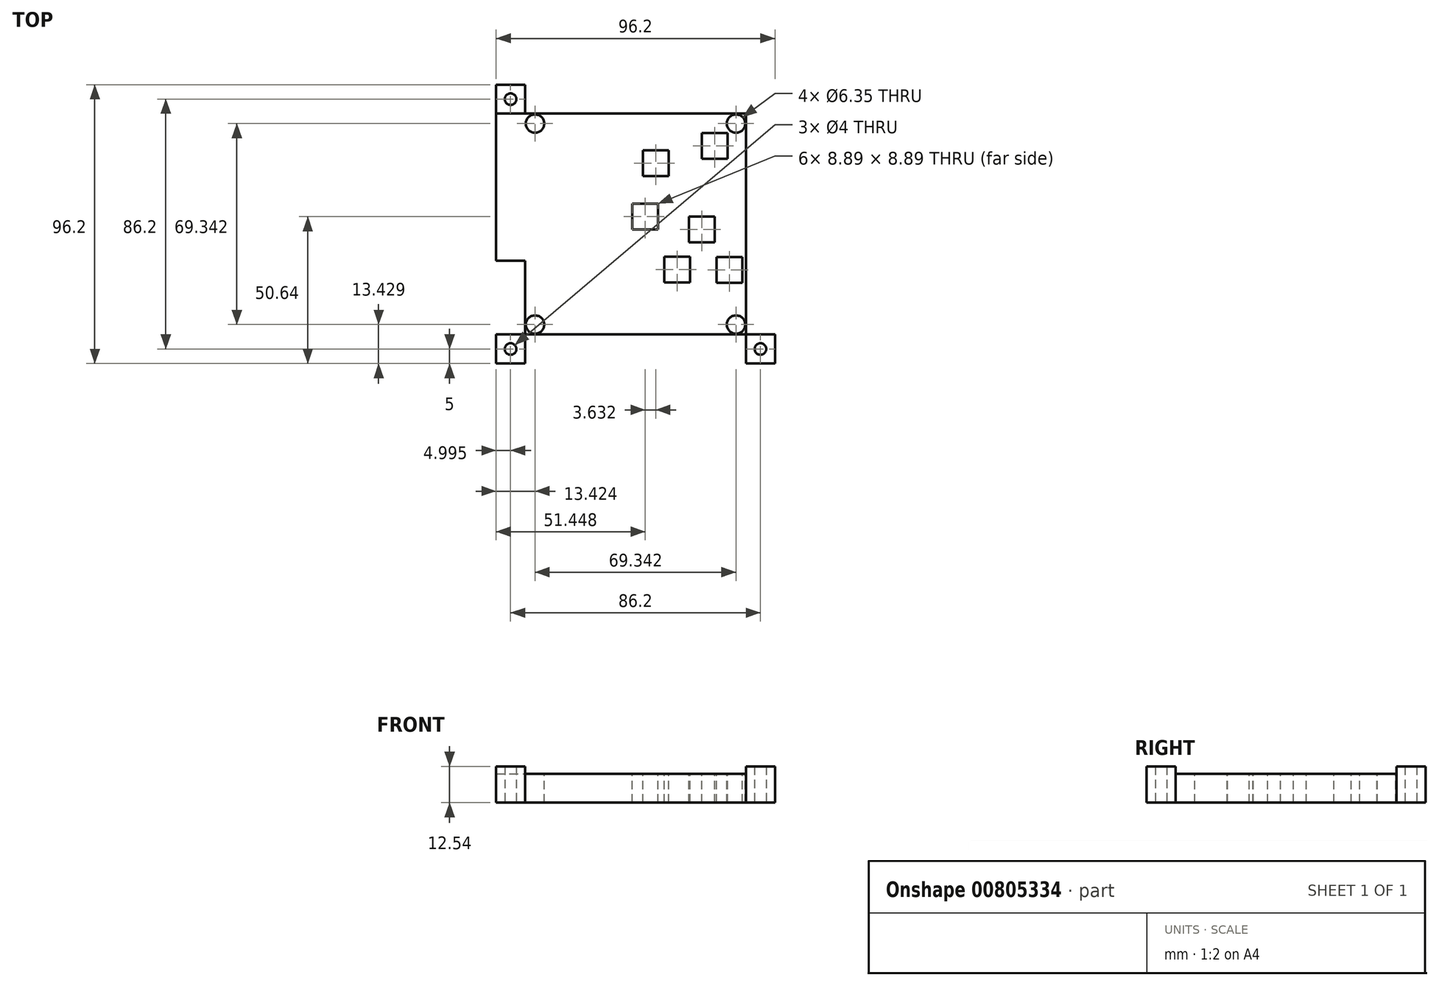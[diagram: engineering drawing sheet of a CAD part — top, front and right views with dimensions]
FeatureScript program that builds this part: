
annotation { "Feature Type Name" : "Feature", "Feature Type Description" : "" }
export const myFeature = defineFeature(function(context is Context, id is Id, definition is map)
    precondition{}
    {
        {
            var Q0;
            Q0=qCreatedBy(makeId("Top.planeOp"),FACE);
            var sketch = newSketch(context, id + "F0", { "sketchPlane" : qUnion([Q0])});
            skLineSegment(sketch, "E0.bottom", {"start": v(-59.12, -65.9) * mm, "end": v(37.08, -65.9) * mm});
            skLineSegment(sketch, "E0.top", {"start": v(-59.12, 30.3) * mm, "end": v(37.08, 30.3) * mm});
            skLineSegment(sketch, "E0.left", {"start": v(-59.12, -65.9) * mm, "end": v(-59.12, 30.3) * mm});
            skLineSegment(sketch, "E0.right", {"start": v(37.08, -65.9) * mm, "end": v(37.08, 30.3) * mm});
            skLineSegment(sketch, "E1.bottom", {"start": v(-59.12, -65.9) * mm, "end": v(-49.12, -65.9) * mm});
            skLineSegment(sketch, "E1.top", {"start": v(-59.12, -55.9) * mm, "end": v(-49.12, -55.9) * mm});
            skLineSegment(sketch, "E1.left", {"start": v(-59.12, -65.9) * mm, "end": v(-59.12, -55.9) * mm});
            skLineSegment(sketch, "E1.right", {"start": v(-49.12, -65.9) * mm, "end": v(-49.12, -55.9) * mm});
            skLineSegment(sketch, "E2.bottom", {"start": v(-49.12, -55.9) * mm, "end": v(27.08, -55.9) * mm});
            skLineSegment(sketch, "E2.top", {"start": v(-49.12, 20.3) * mm, "end": v(27.08, 20.3) * mm});
            skLineSegment(sketch, "E2.left", {"start": v(-49.12, -55.9) * mm, "end": v(-49.12, 20.3) * mm});
            skLineSegment(sketch, "E2.right", {"start": v(27.08, -55.9) * mm, "end": v(27.08, 20.3) * mm});
            skLineSegment(sketch, "E3.bottom", {"start": v(37.08, -65.9) * mm, "end": v(27.08, -65.9) * mm});
            skLineSegment(sketch, "E3.top", {"start": v(37.08, -55.9) * mm, "end": v(27.08, -55.9) * mm});
            skLineSegment(sketch, "E3.left", {"start": v(37.08, -65.9) * mm, "end": v(37.08, -55.9) * mm});
            skLineSegment(sketch, "E3.right", {"start": v(27.08, -65.9) * mm, "end": v(27.08, -55.9) * mm});
            skLineSegment(sketch, "E4.bottom", {"start": v(37.08, 30.3) * mm, "end": v(27.08, 30.3) * mm});
            skLineSegment(sketch, "E4.top", {"start": v(37.08, 20.3) * mm, "end": v(27.08, 20.3) * mm});
            skLineSegment(sketch, "E4.left", {"start": v(37.08, 30.3) * mm, "end": v(37.08, 20.3) * mm});
            skLineSegment(sketch, "E4.right", {"start": v(27.08, 30.3) * mm, "end": v(27.08, 20.3) * mm});
            skLineSegment(sketch, "E5.bottom", {"start": v(-59.12, 30.3) * mm, "end": v(-49.12, 30.3) * mm});
            skLineSegment(sketch, "E5.top", {"start": v(-59.12, 20.3) * mm, "end": v(-49.12, 20.3) * mm});
            skLineSegment(sketch, "E5.left", {"start": v(-59.12, 30.3) * mm, "end": v(-59.12, 20.3) * mm});
            skLineSegment(sketch, "E5.right", {"start": v(-49.12, 30.3) * mm, "end": v(-49.12, 20.3) * mm});
            skLineSegment(sketch, "E6.bottom", {"start": v(-59.12, 20.3) * mm, "end": v(-54.12, 20.3) * mm});
            skLineSegment(sketch, "E6.left", {"start": v(-59.12, 20.3) * mm, "end": v(-59.12, 25.3) * mm});
            skLineSegment(sketch, "E7.bottom", {"start": v(37.08, 20.3) * mm, "end": v(32.08, 20.3) * mm});
            skLineSegment(sketch, "E7.left", {"start": v(37.08, 20.3) * mm, "end": v(37.08, 25.3) * mm});
            skLineSegment(sketch, "E8.bottom", {"start": v(-59.12, -65.9) * mm, "end": v(-54.12, -65.9) * mm});
            skLineSegment(sketch, "E8.left", {"start": v(-59.12, -65.9) * mm, "end": v(-59.12, -60.9) * mm});
            skLineSegment(sketch, "E9.bottom", {"start": v(37.08, -65.9) * mm, "end": v(32.08, -65.9) * mm});
            skLineSegment(sketch, "E9.left", {"start": v(37.08, -65.9) * mm, "end": v(37.08, -60.9) * mm});
            skCircle(sketch, "E10", {"center": v(-54.12, 25.3) * mm, "radius": 2 * mm});
            skCircle(sketch, "E11", {"center": v(32.08, 25.3) * mm, "radius": 2 * mm});
            skCircle(sketch, "E12", {"center": v(-54.12, -60.9) * mm, "radius": 2 * mm});
            skCircle(sketch, "E13", {"center": v(32.08, -60.9) * mm, "radius": 2 * mm});
            skLineSegment(sketch, "E14.left", {"start": v(-49.12, -55.9) * mm, "end": v(-49.12, -55.65) * mm});
            skLineSegment(sketch, "E14.right", {"start": v(27.08, -55.9) * mm, "end": v(27.08, -55.65) * mm});
            skLineSegment(sketch, "E15.bottom", {"start": v(-49.12, 20.3) * mm, "end": v(-48.87, 20.3) * mm});
            skLineSegment(sketch, "E15.top", {"start": v(-49.12, -55.9) * mm, "end": v(-48.87, -55.9) * mm});
            skLineSegment(sketch, "E16.left", {"start": v(-49.12, 20.3) * mm, "end": v(-49.12, 20.05) * mm});
            skLineSegment(sketch, "E16.right", {"start": v(27.08, 20.3) * mm, "end": v(27.08, 20.05) * mm});
            skLineSegment(sketch, "E17.bottom", {"start": v(27.08, 20.3) * mm, "end": v(26.82, 20.3) * mm});
            skLineSegment(sketch, "E17.top", {"start": v(27.08, -55.9) * mm, "end": v(26.82, -55.9) * mm});
            skLineSegment(sketch, "E17.left", {"start": v(27.08, 20.3) * mm, "end": v(27.08, -55.9) * mm});
            skLineSegment(sketch, "E18.bottom", {"start": v(-49.12, -55.9) * mm, "end": v(-45.19, -55.9) * mm});
            skLineSegment(sketch, "E19.left", {"start": v(-49.12, -55.9) * mm, "end": v(-49.12, -54.15) * mm});
            skLineSegment(sketch, "E20.left", {"start": v(-49.12, -55.9) * mm, "end": v(-49.12, -51.96) * mm});
            skLineSegment(sketch, "E21.left", {"start": v(27.08, -55.9) * mm, "end": v(27.08, -51.96) * mm});
            skLineSegment(sketch, "E22.bottom", {"start": v(27.2, -55.9) * mm, "end": v(27.08, -55.9) * mm});
            skLineSegment(sketch, "E23.bottom", {"start": v(27.08, -55.9) * mm, "end": v(23.14, -55.9) * mm});
            skLineSegment(sketch, "E24.left", {"start": v(-49.12, 20.3) * mm, "end": v(-49.12, 16.36) * mm});
            skLineSegment(sketch, "E25.bottom", {"start": v(-49.12, 20.3) * mm, "end": v(-45.19, 20.3) * mm});
            skLineSegment(sketch, "E26.bottom", {"start": v(27.32, 20.3) * mm, "end": v(27.08, 20.3) * mm});
            skLineSegment(sketch, "E26.left", {"start": v(27.08, 20.43) * mm, "end": v(27.08, 20.3) * mm});
            skLineSegment(sketch, "E26.right", {"start": v(27.32, 20.43) * mm, "end": v(27.32, 20.3) * mm});
            skLineSegment(sketch, "E27.left", {"start": v(27.08, 20.3) * mm, "end": v(27.08, 16.36) * mm});
            skLineSegment(sketch, "E28.top", {"start": v(27.08, 20.3) * mm, "end": v(23.14, 20.3) * mm});
            skLineSegment(sketch, "E28.left", {"start": v(27.08, 20.05) * mm, "end": v(27.08, 20.3) * mm});
            skCircle(sketch, "E29", {"center": v(-45.7, 16.87) * mm, "radius": 3.18 * mm});
            skCircle(sketch, "E30", {"center": v(23.65, -52.47) * mm, "radius": 3.18 * mm});
            skCircle(sketch, "E31", {"center": v(23.65, 16.87) * mm, "radius": 3.18 * mm});
            skCircle(sketch, "E32", {"center": v(-45.7, -52.47) * mm, "radius": 3.17 * mm});
            skLineSegment(sketch, "E33.bottom", {"start": v(27.08, -55.9) * mm, "end": v(-0.86, -55.9) * mm});
            skLineSegment(sketch, "E33.left", {"start": v(27.08, -55.9) * mm, "end": v(27.08, -1.3) * mm});
            skLineSegment(sketch, "E34.bottom", {"start": v(0.4, -1.3) * mm, "end": v(-8.48, -1.3) * mm});
            skLineSegment(sketch, "E34.top", {"start": v(0.4, 7.6) * mm, "end": v(-8.48, 7.6) * mm});
            skLineSegment(sketch, "E34.left", {"start": v(0.4, -1.3) * mm, "end": v(0.4, 7.6) * mm});
            skLineSegment(sketch, "E34.right", {"start": v(-8.48, -1.3) * mm, "end": v(-8.48, 7.6) * mm});
            skLineSegment(sketch, "E35.bottom", {"start": v(27.08, -55.9) * mm, "end": v(-4.5, -55.9) * mm});
            skLineSegment(sketch, "E35.left", {"start": v(27.08, -55.9) * mm, "end": v(27.08, -19.7) * mm});
            skLineSegment(sketch, "E36.bottom", {"start": v(-3.23, -19.7) * mm, "end": v(-12.12, -19.7) * mm});
            skLineSegment(sketch, "E36.top", {"start": v(-3.23, -10.82) * mm, "end": v(-12.12, -10.82) * mm});
            skLineSegment(sketch, "E36.left", {"start": v(-3.23, -19.7) * mm, "end": v(-3.23, -10.82) * mm});
            skLineSegment(sketch, "E36.right", {"start": v(-12.12, -19.7) * mm, "end": v(-12.12, -10.82) * mm});
            skLineSegment(sketch, "E37.bottom", {"start": v(27.08, -55.9) * mm, "end": v(6.55, -55.9) * mm});
            skLineSegment(sketch, "E37.left", {"start": v(27.08, -55.9) * mm, "end": v(27.08, -38) * mm});
            skLineSegment(sketch, "E38.bottom", {"start": v(7.82, -38) * mm, "end": v(-1.07, -38) * mm});
            skLineSegment(sketch, "E38.top", {"start": v(7.82, -29.1) * mm, "end": v(-1.07, -29.1) * mm});
            skLineSegment(sketch, "E38.left", {"start": v(7.82, -38) * mm, "end": v(7.82, -29.1) * mm});
            skLineSegment(sketch, "E38.right", {"start": v(-1.07, -38) * mm, "end": v(-1.07, -29.1) * mm});
            skLineSegment(sketch, "E39.bottom", {"start": v(27.08, -55.9) * mm, "end": v(23.52, -55.9) * mm});
            skLineSegment(sketch, "E39.left", {"start": v(27.08, -55.9) * mm, "end": v(27.08, 4.7) * mm});
            skLineSegment(sketch, "E40.bottom", {"start": v(20.73, 4.7) * mm, "end": v(11.84, 4.7) * mm});
            skLineSegment(sketch, "E40.top", {"start": v(20.73, 13.6) * mm, "end": v(11.84, 13.6) * mm});
            skLineSegment(sketch, "E40.left", {"start": v(11.84, 4.7) * mm, "end": v(11.84, 13.6) * mm});
            skLineSegment(sketch, "E40.right", {"start": v(20.73, 4.7) * mm, "end": v(20.73, 13.6) * mm});
            skPoint(sketch, "E41.oppositeSnap0", {"position": v(16.28, 13.6) * mm});
            skLineSegment(sketch, "E41.bottom", {"start": v(27.08, -55.9) * mm, "end": v(24.54, -55.9) * mm});
            skLineSegment(sketch, "E41.left", {"start": v(27.08, -55.9) * mm, "end": v(27.08, -24.15) * mm});
            skLineSegment(sketch, "E42.bottom", {"start": v(16.28, -24.15) * mm, "end": v(7.4, -24.15) * mm});
            skLineSegment(sketch, "E42.top", {"start": v(16.28, -15.26) * mm, "end": v(7.4, -15.26) * mm});
            skLineSegment(sketch, "E42.left", {"start": v(16.28, -24.15) * mm, "end": v(16.28, -15.26) * mm});
            skLineSegment(sketch, "E42.right", {"start": v(7.4, -24.15) * mm, "end": v(7.4, -15.26) * mm});
            skLineSegment(sketch, "E43.bottom", {"start": v(27.08, -55.9) * mm, "end": v(26.57, -55.9) * mm});
            skLineSegment(sketch, "E43.left", {"start": v(27.08, -55.9) * mm, "end": v(27.08, -38.12) * mm});
            skLineSegment(sketch, "E44.bottom", {"start": v(25.8, -38.12) * mm, "end": v(16.92, -38.12) * mm});
            skLineSegment(sketch, "E44.top", {"start": v(25.8, -29.23) * mm, "end": v(16.92, -29.23) * mm});
            skLineSegment(sketch, "E44.left", {"start": v(25.8, -38.12) * mm, "end": v(25.8, -29.23) * mm});
            skLineSegment(sketch, "E44.right", {"start": v(16.92, -38.12) * mm, "end": v(16.92, -29.23) * mm});
            skLineSegment(sketch, "E45.top", {"start": v(-59.12, -30.5) * mm, "end": v(-49.12, -30.5) * mm});
            skLineSegment(sketch, "E45.left", {"start": v(-59.12, 20.3) * mm, "end": v(-59.12, -30.5) * mm});
            skLineSegment(sketch, "E45.right", {"start": v(-49.12, 20.3) * mm, "end": v(-49.12, -30.5) * mm});
            skLineSegment(sketch, "E46", {"start": v(27.08, -38.12) * mm, "end": v(25.8, -38.12) * mm});
            skSolve(sketch);
        }
        {
            var Q0;
            Q0=makeQuery(id+"F0.imprint","IMPRINT",FACE,{"disambiguationData":[TD([[makeQuery(id+"F0.imprint","IMPRINT",EDGE,{"derivedFrom":sQuery(id+"F0.wireOp",EDGE,"E0.top")}),-1.0]])]});
            var Q1;
            Q1=makeQuery(id+"F0.imprint","IMPRINT",FACE,{"disambiguationData":[TD([[makeQuery(id+"F0.imprint","IMPRINT",EDGE,{"derivedFrom":sQuery(id+"F0.wireOp",EDGE,"E5.bottom")}),-1.0]])]});
            var Q2;
            Q2=makeQuery(id+"F0.imprint","IMPRINT",FACE,{"disambiguationData":[TD([[makeQuery(id+"F0.imprint","IMPRINT",EDGE,{"derivedFrom":sQuery(id+"F0.wireOp",EDGE,"E0.left")}),-1.0]])]});
            var Q3;
            Q3=makeQuery(id+"F0.imprint","IMPRINT",FACE,{"disambiguationData":[TD([[makeQuery(id+"F0.imprint","IMPRINT",EDGE,{"derivedFrom":sQuery(id+"F0.wireOp",EDGE,"E0.right")}),1.0]])]});
            var Q4;
            Q4=makeQuery(id+"F0.imprint","IMPRINT",FACE,{"disambiguationData":[TD([[makeQuery(id+"F0.imprint","IMPRINT",EDGE,{"derivedFrom":sQuery(id+"F0.wireOp",EDGE,"E4.bottom")}),1.0]])]});
            var Q5;
            Q5=makeQuery(id+"F0.imprint","IMPRINT",FACE,{"disambiguationData":[TD([[makeQuery(id+"F0.imprint","IMPRINT",EDGE,{"derivedFrom":sQuery(id+"F0.wireOp",EDGE,"E3.bottom")}),-1.0]])]});
            var Q6;
            Q6=makeQuery(id+"F0.imprint","IMPRINT",FACE,{"disambiguationData":[TD([[makeQuery(id+"F0.imprint","IMPRINT",EDGE,{"derivedFrom":sQuery(id+"F0.wireOp",EDGE,"E0.bottom")}),1.0]])]});
            var Q7;
            Q7=makeQuery(id+"F0.imprint","IMPRINT",FACE,{"disambiguationData":[TD([[makeQuery(id+"F0.imprint","IMPRINT",EDGE,{"derivedFrom":sQuery(id+"F0.wireOp",EDGE,"E1.bottom")}),1.0]])]});
            extrude(context, id + "F1", {"entities" : qUnion([Q0, Q1, Q2, Q3, Q4, Q5, Q6, Q7]), "depth" : 2.54 * mm, "offsetDistance" : 25.4 * mm});
        }
        {
            var Q0;
            Q0=makeQuery(id+"F0.imprint","IMPRINT",FACE,{"disambiguationData":[TD([[makeQuery(id+"F0.imprint","IMPRINT",EDGE,{"derivedFrom":sQuery(id+"F0.wireOp",EDGE,"E4.bottom")}),1.0]])]});
            var Q1;
            Q1=makeQuery(id+"F0.imprint","IMPRINT",FACE,{"disambiguationData":[TD([[makeQuery(id+"F0.imprint","IMPRINT",EDGE,{"derivedFrom":sQuery(id+"F0.wireOp",EDGE,"E0.right")}),1.0]])]});
            var Q2;
            Q2=makeQuery(id+"F0.imprint","IMPRINT",FACE,{"disambiguationData":[TD([[makeQuery(id+"F0.imprint","IMPRINT",EDGE,{"derivedFrom":sQuery(id+"F0.wireOp",EDGE,"E0.top")}),-1.0]])]});
            var Q3;
            Q3=makeQuery(id+"F0.imprint","IMPRINT",FACE,{"disambiguationData":[TD([[makeQuery(id+"F0.imprint","IMPRINT",EDGE,{"derivedFrom":sQuery(id+"F0.wireOp",EDGE,"E5.bottom")}),-1.0]])]});
            var Q4;
            {var subQ1=sQuery(id+"F0.wireOp",EDGE,"E45.top");Q4=makeQuery(id+"F0.imprint","IMPRINT",FACE,{"disambiguationData":[TD([[makeQuery(id+"F0.imprint","IMPRINT",EDGE,{"derivedFrom":subQ1}),1.0]])]});}
            var Q5;
            Q5=makeQuery(id+"F0.imprint","IMPRINT",FACE,{"disambiguationData":[TD([[makeQuery(id+"F0.imprint","IMPRINT",EDGE,{"derivedFrom":sQuery(id+"F0.wireOp",EDGE,"E0.left")}),-1.0]])]});
            var Q6;
            Q6=makeQuery(id+"F0.imprint","IMPRINT",FACE,{"disambiguationData":[TD([[makeQuery(id+"F0.imprint","IMPRINT",EDGE,{"derivedFrom":sQuery(id+"F0.wireOp",EDGE,"E1.bottom")}),1.0]])]});
            var Q7;
            Q7=makeQuery(id+"F0.imprint","IMPRINT",FACE,{"disambiguationData":[TD([[makeQuery(id+"F0.imprint","IMPRINT",EDGE,{"derivedFrom":sQuery(id+"F0.wireOp",EDGE,"E0.bottom")}),1.0]])]});
            var Q8;
            Q8=makeQuery(id+"F0.imprint","IMPRINT",FACE,{"disambiguationData":[TD([[makeQuery(id+"F0.imprint","IMPRINT",EDGE,{"derivedFrom":sQuery(id+"F0.wireOp",EDGE,"E3.bottom")}),-1.0]])]});
            var Q9;
            {var subQ23=sQuery(id+"F0.wireOp",EDGE,"E2.left");Q9=makeQuery(id+"F0.imprint","IMPRINT",FACE,{"disambiguationData":[TD([[makeQuery(id+"F0.imprint","IMPRINT",EDGE,{"derivedFrom":subQ23}),-1.0]])]});}
            extrude(context, id + "F2", {"entities" : qUnion([Q0, Q1, Q2, Q3, Q4, Q5, Q6, Q7, Q8, Q9]), "operationType" : NewBodyOperationType.ADD, "oppositeDirection" : true, "depth" : 10 * mm, "offsetDistance" : 25.4 * mm});
        }
    });
